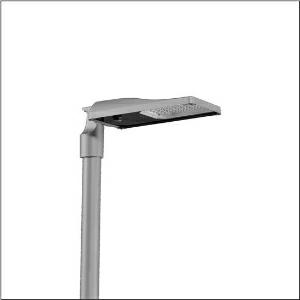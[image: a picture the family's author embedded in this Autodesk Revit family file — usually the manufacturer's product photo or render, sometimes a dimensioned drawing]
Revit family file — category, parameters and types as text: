
# Revit family: streetlight_sl_31_mini___st1_0a_5xh2d31r08ga_f9bd
name_source: partatom
category: Lighting Fixtures
units: mm (PartAtom-declared; Revit-internal decimal feet)

## family parameters
Cut with Voids When Loaded = No
Host = Face
Light Source = No
Part Type = Normal
Room Calculation Point = No
Round Connector Dimension = Use Diameter
Shared = No

## types (1)
- --- (1 x LED, 5880 lm, 39.3 W, 3000K)
    Apparent Load = 39 VA
    CIE Flux Codes = 37 72 97 100 100
    Color Rendering = 70
    Color Temperature = 3000K
    Default Elevation = 1800 mm
    Description = Streetlight SL 31 mini D4i, Desk-Remote mast luminaire for post-top, side-entry; light control with lens of PMMA; light distribution: ST1.0a, direct asymmetric distribution, for standard-compliant lighting for roads and squares; LED: luminous flux: 5.880lm, light colour: 730, colour temperature: 3000K; luminous efficacy: 149,6lm/W; control: pre-setting: logarithmic dimming characteristic, flexible luminous flux parameterisation, time-dependent luminous flux control, constant luminous flux control, power reduction, intelligent temperature release in ECG and LED module, overheat protection; luminaire housing, of diecast aluminium, Siteco® metallic grey (DB 702S), corrosivity category C5 high according to DIN EN ISO 12944; cover of toughened safety glass, transparent, mast flange of diecast aluminium, Siteco® metallic grey (DB 702S), spigot size: 76/60mm, mast flange included unmounted; with cable H07RN-F 2x 1.5mm², cable length: 6,5m, connection cable pre-assembled; mains connection: 220..240V, AC, 50/60Hz; power consumption (at start of service life): 39,3W / (at end of service life): 40,7W / (with reduced operation 50%): 18,1W; protection rating (complete): IP66; insulation class (complete): insulation class II (safety insulation); impact resistance: IK09; certification: CE, ENEC, ENEC+, VDE, UKCA, ZD4i; permissible operating ambient temperature for outdoor applications: -40..+50°C; packaging unit: 1 piece

Light Distribution: ST1.0a
    Height = 76 mm
    Lamp = 1 x LED
    Lamp Light Flux = 5880 lm
    Lamp Power = 39.3 W
    Lamp count = 1
    Length = 547 mm
    Luminous efficacy = 150 lm/W
    Manufacturer = Siteco
    ModVariant = No
    Model = 5XH2D31R08GA
    Number of Poles = 1
    OnlyDefault = Yes
    Power Factor = 1
    Product Name = Streetlight SL 31 mini | ST1.0a
    Product group = mast luminaire | pylon top
    ProductGroupID = 6100
    Protection Class = Protection class II
    Protection Degree = IP 66
    RLX_Detail_Level = 1
    RLX_Emergency_Light_Flux = 0 lm
    RLX_Emergency_Type = 0
    RLX_Emergency_Type_DB = No
    RlxData = <blob elided: 39661 chars, md5=793806cc>
    Socket = socket
    Standby Power = 0 W
    System Light Flux = 5880 lm
    System Power = 39 W
    Type Comments = factory setting: luminous flux: 100 % | dim-lin: 254 | 798 mA
    Type Image = l_1300328.jpg
    URL = http://relux.com
    VarID = @adj_075255
    Voltage = 0 V
    Weight = 0.00 kg
    Width = 265 mm

## geometry (parser evidence)
native form markers: Blend x4, Sweep x10
no freeform markers — native parametric forms only
